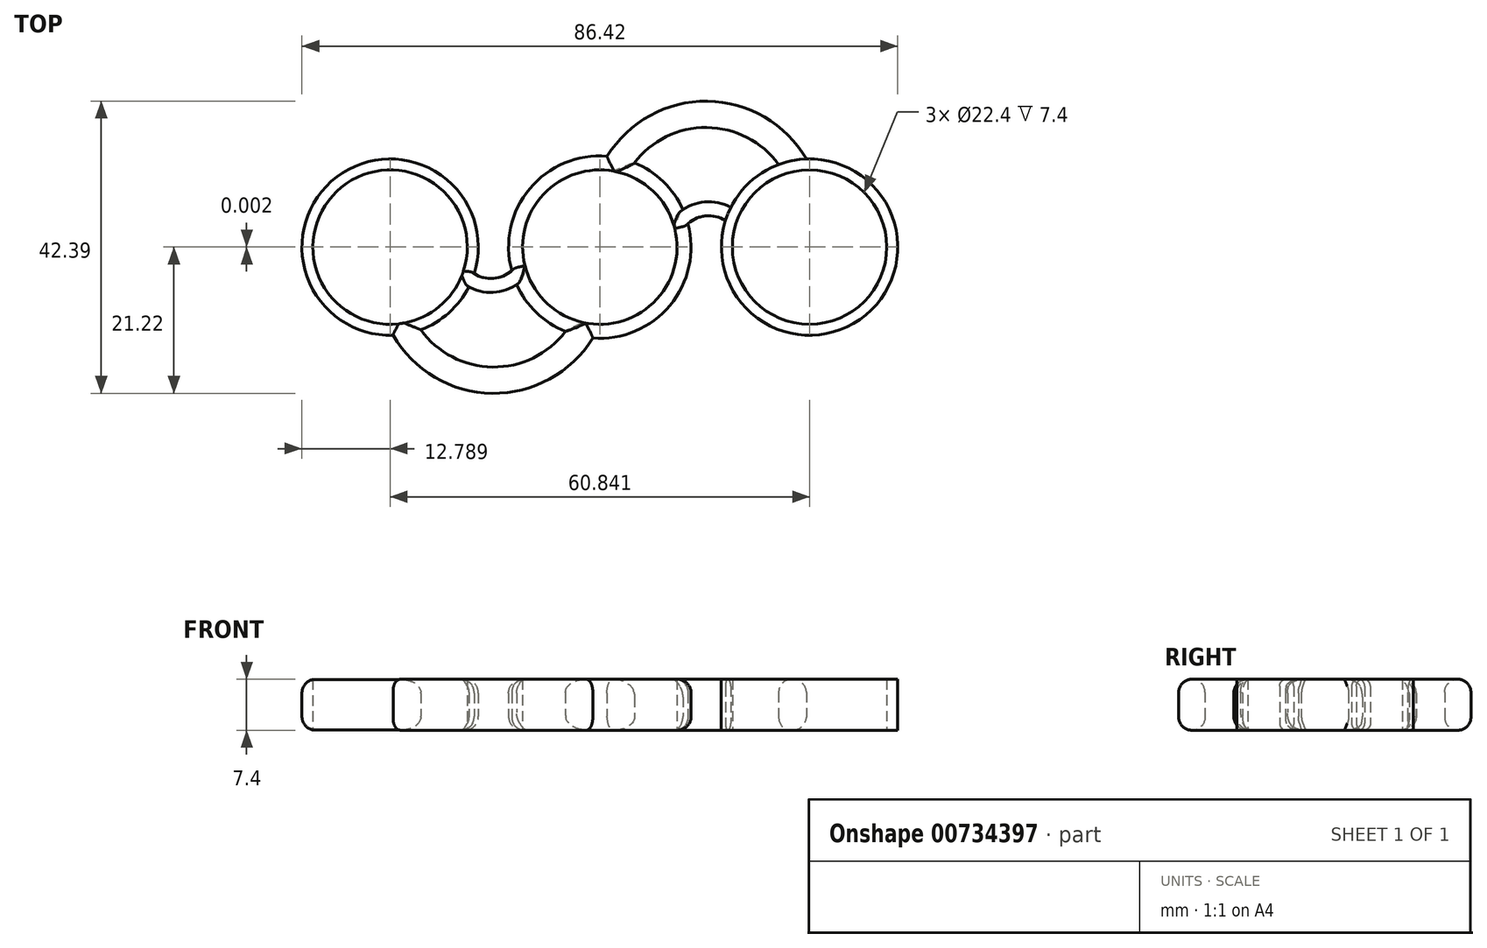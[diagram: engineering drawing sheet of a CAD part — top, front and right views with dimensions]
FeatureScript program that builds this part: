
annotation { "Feature Type Name" : "Feature", "Feature Type Description" : "" }
export const myFeature = defineFeature(function(context is Context, id is Id, definition is map)
    precondition{}
    {
        {
            var Q0;
            Q0=qCreatedBy(makeId("Top.planeOp"),FACE);
            var sketch = newSketch(context, id + "F0", { "sketchPlane" : qUnion([Q0])});
            skCircle(sketch, "E0", {"center": v(0, 0) * mm, "radius": 11.2 * mm});
            skArc(sketch, "E1", {"start": v(-22.34, -1.14) * mm, "mid": v(-15.23, -6.55) * mm, "end": v(-9.15, 0) * mm});
            skArc(sketch, "E2.0", {"start": v(-20.42, 0.11) * mm, "mid": v(-15.8, -4.55) * mm, "end": v(-11.18, 0.11) * mm});
            skLineSegment(sketch, "E3", {"start": v(0, 34.2) * mm, "end": v(0, -29.02) * mm});
            skArc(sketch, "E4.MirrorCS", {"start": v(20.42, 0.11) * mm, "mid": v(20.42, 0.06) * mm, "end": v(20.42, 0) * mm});
            skLineSegment(sketch, "E5", {"start": v(-20.42, 0.11) * mm, "end": v(-22.45, 0) * mm});
            skLineSegment(sketch, "E6", {"start": v(-11.18, 0.11) * mm, "end": v(-9.15, 0) * mm});
            skLineSegment(sketch, "E7", {"start": v(9.15, 0) * mm, "end": v(11.2, 0) * mm});
            skArc(sketch, "E8.MirrorCS", {"start": v(20.42, -0.11) * mm, "mid": v(15.8, 4.55) * mm, "end": v(11.18, -0.11) * mm});
            skArc(sketch, "E9.MirrorCS", {"start": v(22.34, 1.14) * mm, "mid": v(15.23, 6.55) * mm, "end": v(9.15, 0) * mm});
            skLineSegment(sketch, "E10.trimOffspring", {"start": v(19.66, 0) * mm, "end": v(22.45, 0) * mm});
            skPoint(sketch, "E11.orphan", {"position": v(7.21, 0) * mm});
            skArc(sketch, "E12.trimOffspring", {"start": v(11.2, -0.32) * mm, "mid": v(11.18, -0.1) * mm, "end": v(11.18, 0.11) * mm});
            skPoint(sketch, "E13.MirrorCS.start.orphan", {"position": v(22.45, 0) * mm});
            skPoint(sketch, "E14.trimOffspring.end.orphan", {"position": v(9.15, 0) * mm});
            skArc(sketch, "E15", {"start": v(30.99, 10.7) * mm, "mid": v(15.66, 21.17) * mm, "end": v(0, 11.2) * mm});
            skArc(sketch, "E16.0", {"start": v(27.46, 9.25) * mm, "mid": v(15.6, 17.36) * mm, "end": v(3.48, 9.64) * mm});
            skArc(sketch, "E17.MirrorCS", {"start": v(-27.46, -9.3) * mm, "mid": v(-15.6, -17.4) * mm, "end": v(-3.48, -9.7) * mm});
            skArc(sketch, "E18.MirrorCS", {"start": v(-30.99, -10.74) * mm, "mid": v(-15.66, -21.22) * mm, "end": v(0, -11.25) * mm});
            skCircle(sketch, "E19.0", {"center": v(0, 0) * mm, "radius": 13.23 * mm});
            skCircle(sketch, "E20.0", {"center": v(-30.42, 0) * mm, "radius": 12.8 * mm});
            skCircle(sketch, "E21.0", {"center": v(30.42, 0) * mm, "radius": 12.8 * mm});
            skPoint(sketch, "E22.0.midPoint", {"position": v(-30.42, 7.25) * mm});
            skLineSegment(sketch, "E23.5", {"start": v(21.85, 0.3) * mm, "end": v(22.34, 1.14) * mm});
            skPoint(sketch, "E23.0.midPoint", {"position": v(30.24, 7.25) * mm});
            skPoint(sketch, "E23.cCircle.center.orphan", {"position": v(30.24, -0.16) * mm});
            skPoint(sketch, "E23.0.start.orphan", {"position": v(26.13, 7.7) * mm});
            skPoint(sketch, "E23.1.start.orphan", {"position": v(34.35, 6.8) * mm});
            skCircle(sketch, "E24.cCircle", {"center": v(-30.42, 0) * mm, "radius": 7.25 * mm, "construction": true});
            skLineSegment(sketch, "E24.0", {"start": v(-34.6, 7.25) * mm, "end": v(-26.23, 7.25) * mm});
            skLineSegment(sketch, "E24.1", {"start": v(-26.23, 7.25) * mm, "end": v(-22.05, 0) * mm});
            skLineSegment(sketch, "E24.2", {"start": v(-22.05, 0) * mm, "end": v(-26.23, -7.25) * mm});
            skLineSegment(sketch, "E24.3", {"start": v(-26.23, -7.25) * mm, "end": v(-34.6, -7.25) * mm});
            skLineSegment(sketch, "E24.4", {"start": v(-34.6, -7.25) * mm, "end": v(-38.8, 0) * mm});
            skLineSegment(sketch, "E24.5", {"start": v(-38.8, 0) * mm, "end": v(-34.6, 7.25) * mm});
            skCircle(sketch, "E25.cCircle", {"center": v(30.42, 0) * mm, "radius": 7.25 * mm, "construction": true});
            skLineSegment(sketch, "E25.0", {"start": v(26.05, 7.15) * mm, "end": v(34.42, 7.35) * mm});
            skLineSegment(sketch, "E25.1", {"start": v(34.42, 7.35) * mm, "end": v(38.79, 0.21) * mm});
            skLineSegment(sketch, "E25.2", {"start": v(38.79, 0.21) * mm, "end": v(34.79, -7.14) * mm});
            skLineSegment(sketch, "E25.3", {"start": v(34.79, -7.14) * mm, "end": v(26.42, -7.35) * mm});
            skLineSegment(sketch, "E25.4", {"start": v(26.42, -7.35) * mm, "end": v(22.05, -0.2) * mm});
            skLineSegment(sketch, "E25.5", {"start": v(22.05, -0.2) * mm, "end": v(26.05, 7.15) * mm});
            skCircle(sketch, "E26", {"center": v(-30.42, 0) * mm, "radius": 11.2 * mm});
            skCircle(sketch, "E27", {"center": v(30.42, 0) * mm, "radius": 11.2 * mm});
            skSolve(sketch);
        }
        {
            var Q0;
            {var subQ0=sQuery(id+"F0.wireOp",EDGE,"E20.0");var subQ1=sQuery(id+"F0.wireOp",EDGE,"E17.MirrorCS");var subQ2=makeQuery(id+"F0.imprint","INTERSECT",VERTEX,{"derivedFrom":[subQ1,subQ0]});Q0=makeQuery(id+"F0.imprint","IMPRINT",FACE,{"disambiguationData":[TD([[makeQuery(id+"F0.imprint","IMPRINT",EDGE,{"disambiguationData":[TD([[subQ2,-1.0]])],"derivedFrom":subQ1}),-1.0]])]});}
            var Q1;
            {var subQ0=sQuery(id+"F0.wireOp",EDGE,"E2.0");var subQ1=sQuery(id+"F0.wireOp",EDGE,"E0");var subQ2=makeQuery(id+"F0.imprint","INTERSECT",VERTEX,{"derivedFrom":[subQ1,subQ0]});Q1=makeQuery(id+"F0.imprint","IMPRINT",FACE,{"disambiguationData":[TD([[makeQuery(id+"F0.imprint","IMPRINT",EDGE,{"disambiguationData":[TD([[subQ2,-1.0]])],"derivedFrom":subQ1}),-1.0]])]});}
            var Q2;
            {var subQ3=sQuery(id+"F0.wireOp",EDGE,"E2.0");var subQ5=sQuery(id+"F0.wireOp",EDGE,"E19.0");var subQ6=makeQuery(id+"F0.imprint","INTERSECT",VERTEX,{"derivedFrom":[subQ3,subQ5]});Q2=makeQuery(id+"F0.imprint","IMPRINT",FACE,{"disambiguationData":[TD([[makeQuery(id+"F0.imprint","IMPRINT",EDGE,{"disambiguationData":[TD([[subQ6,-1.0]])],"derivedFrom":subQ3}),1.0]])]});}
            var Q3;
            {var subQ0=sQuery(id+"F0.wireOp",EDGE,"E16.0");var subQ1=sQuery(id+"F0.wireOp",EDGE,"E0");var subQ2=makeQuery(id+"F0.imprint","INTERSECT",VERTEX,{"derivedFrom":[subQ1,subQ0]});Q3=makeQuery(id+"F0.imprint","IMPRINT",FACE,{"disambiguationData":[TD([[makeQuery(id+"F0.imprint","IMPRINT",EDGE,{"disambiguationData":[TD([[subQ2,1.0]])],"derivedFrom":subQ1}),-1.0]])]});}
            var Q4;
            {var subQ0=sQuery(id+"F0.wireOp",EDGE,"E8.MirrorCS");var subQ1=sQuery(id+"F0.wireOp",EDGE,"E0");var subQ2=makeQuery(id+"F0.imprint","INTERSECT",VERTEX,{"derivedFrom":[subQ1,subQ0]});Q4=makeQuery(id+"F0.imprint","IMPRINT",FACE,{"disambiguationData":[TD([[makeQuery(id+"F0.imprint","IMPRINT",EDGE,{"disambiguationData":[TD([[subQ2,-1.0]])],"derivedFrom":subQ1}),-1.0]])]});}
            var Q5;
            {var subQ1=sQuery(id+"F0.wireOp",EDGE,"E0");var subQ3=sQuery(id+"F0.wireOp",EDGE,"E17.MirrorCS");var subQ4=makeQuery(id+"F0.imprint","INTERSECT",VERTEX,{"derivedFrom":[subQ1,subQ3]});Q5=makeQuery(id+"F0.imprint","IMPRINT",FACE,{"disambiguationData":[TD([[makeQuery(id+"F0.imprint","IMPRINT",EDGE,{"disambiguationData":[TD([[subQ4,1.0]])],"derivedFrom":subQ3}),-1.0]])]});}
            var Q6;
            {var subQ0=sQuery(id+"F0.wireOp",EDGE,"E17.MirrorCS");var subQ1=sQuery(id+"F0.wireOp",EDGE,"E0");var subQ2=makeQuery(id+"F0.imprint","INTERSECT",VERTEX,{"derivedFrom":[subQ1,subQ0]});Q6=makeQuery(id+"F0.imprint","IMPRINT",FACE,{"disambiguationData":[TD([[makeQuery(id+"F0.imprint","IMPRINT",EDGE,{"disambiguationData":[TD([[subQ2,1.0]])],"derivedFrom":subQ1}),-1.0]])]});}
            var Q7;
            {var subQ0=sQuery(id+"F0.wireOp",EDGE,"E0");var subQ1=makeQuery(id+"F0.imprint","INTERSECT",VERTEX,{"derivedFrom":[subQ0,sQuery(id+"F0.wireOp",EDGE,"E7")]});Q7=makeQuery(id+"F0.imprint","IMPRINT",FACE,{"disambiguationData":[TD([[makeQuery(id+"F0.imprint","IMPRINT",EDGE,{"disambiguationData":[TD([[subQ1,-1.0]])],"derivedFrom":subQ0}),-1.0]])]});}
            var Q8;
            {var subQ1=sQuery(id+"F0.wireOp",EDGE,"E3");var subQ3=sQuery(id+"F0.wireOp",EDGE,"E19.0");var subQ4=makeQuery(id+"F0.imprint","INTERSECT",VERTEX,{"disambiguationData":[OD(1.0)],"derivedFrom":[subQ1,subQ3]});Q8=makeQuery(id+"F0.imprint","IMPRINT",FACE,{"disambiguationData":[TD([[makeQuery(id+"F0.imprint","IMPRINT",EDGE,{"disambiguationData":[TD([[subQ4,1.0]])],"derivedFrom":subQ3}),1.0]])]});}
            var Q9;
            {var subQ1=sQuery(id+"F0.wireOp",EDGE,"E0");var subQ3=sQuery(id+"F0.wireOp",EDGE,"E16.0");var subQ4=makeQuery(id+"F0.imprint","INTERSECT",VERTEX,{"derivedFrom":[subQ1,subQ3]});Q9=makeQuery(id+"F0.imprint","IMPRINT",FACE,{"disambiguationData":[TD([[makeQuery(id+"F0.imprint","IMPRINT",EDGE,{"disambiguationData":[TD([[subQ4,1.0]])],"derivedFrom":subQ3}),-1.0]])]});}
            var Q10;
            {var subQ1=sQuery(id+"F0.wireOp",EDGE,"E3");var subQ3=sQuery(id+"F0.wireOp",EDGE,"E19.0");var subQ4=makeQuery(id+"F0.imprint","INTERSECT",VERTEX,{"disambiguationData":[OD(0.0)],"derivedFrom":[subQ1,subQ3]});Q10=makeQuery(id+"F0.imprint","IMPRINT",FACE,{"disambiguationData":[TD([[makeQuery(id+"F0.imprint","IMPRINT",EDGE,{"disambiguationData":[TD([[subQ4,1.0]])],"derivedFrom":subQ3}),1.0]])]});}
            var Q11;
            {var subQ0=sQuery(id+"F0.wireOp",EDGE,"E21.0");var subQ1=sQuery(id+"F0.wireOp",EDGE,"E15");var subQ2=makeQuery(id+"F0.imprint","INTERSECT",VERTEX,{"derivedFrom":[subQ1,subQ0]});Q11=makeQuery(id+"F0.imprint","IMPRINT",FACE,{"disambiguationData":[TD([[makeQuery(id+"F0.imprint","IMPRINT",EDGE,{"disambiguationData":[TD([[subQ2,-1.0]])],"derivedFrom":subQ1}),1.0]])]});}
            var Q12;
            {var subQ0=sQuery(id+"F0.wireOp",EDGE,"E23.5");Q12=makeQuery(id+"F0.imprint","IMPRINT",FACE,{"disambiguationData":[TD([[makeQuery(id+"F0.imprint","IMPRINT",EDGE,{"derivedFrom":subQ0}),-1.0]])]});}
            var Q13;
            {var subQ7=sQuery(id+"F0.wireOp",EDGE,"E23.5");Q13=makeQuery(id+"F0.imprint","IMPRINT",FACE,{"disambiguationData":[TD([[makeQuery(id+"F0.imprint","IMPRINT",EDGE,{"derivedFrom":subQ7}),1.0]])]});}
            var Q14;
            {var subQ0=sQuery(id+"F0.wireOp",EDGE,"E21.0");var subQ1=sQuery(id+"F0.wireOp",EDGE,"E8.MirrorCS");var subQ2=makeQuery(id+"F0.imprint","INTERSECT",VERTEX,{"derivedFrom":[subQ1,subQ0]});Q14=makeQuery(id+"F0.imprint","IMPRINT",FACE,{"disambiguationData":[TD([[makeQuery(id+"F0.imprint","IMPRINT",EDGE,{"disambiguationData":[TD([[subQ2,-1.0]])],"derivedFrom":subQ1}),-1.0]])]});}
            var Q15;
            {var subQ0=sQuery(id+"F0.wireOp",EDGE,"E20.0");var subQ1=sQuery(id+"F0.wireOp",EDGE,"E1");var subQ2=makeQuery(id+"F0.imprint","INTERSECT",VERTEX,{"derivedFrom":[subQ1,subQ0]});Q15=makeQuery(id+"F0.imprint","IMPRINT",FACE,{"disambiguationData":[TD([[makeQuery(id+"F0.imprint","IMPRINT",EDGE,{"disambiguationData":[TD([[subQ2,-1.0]])],"derivedFrom":subQ1}),1.0]])]});}
            var Q16;
            {var subQ0=sQuery(id+"F0.wireOp",EDGE,"E26");var subQ1=sQuery(id+"F0.wireOp",EDGE,"E1");var subQ2=makeQuery(id+"F0.imprint","INTERSECT",VERTEX,{"derivedFrom":[subQ1,subQ0]});Q16=makeQuery(id+"F0.imprint","IMPRINT",FACE,{"disambiguationData":[TD([[makeQuery(id+"F0.imprint","IMPRINT",EDGE,{"disambiguationData":[TD([[subQ2,-1.0]])],"derivedFrom":subQ1}),1.0]])]});}
            var Q17;
            {var subQ0=sQuery(id+"F0.wireOp",EDGE,"E26");var subQ1=sQuery(id+"F0.wireOp",EDGE,"E1");var subQ2=makeQuery(id+"F0.imprint","INTERSECT",VERTEX,{"derivedFrom":[subQ1,subQ0]});Q17=makeQuery(id+"F0.imprint","IMPRINT",FACE,{"disambiguationData":[TD([[makeQuery(id+"F0.imprint","IMPRINT",EDGE,{"disambiguationData":[TD([[subQ2,-1.0]])],"derivedFrom":subQ1}),-1.0]])]});}
            var Q18;
            {var subQ0=sQuery(id+"F0.wireOp",EDGE,"E26");var subQ1=sQuery(id+"F0.wireOp",EDGE,"E17.MirrorCS");var subQ2=makeQuery(id+"F0.imprint","INTERSECT",VERTEX,{"derivedFrom":[subQ1,subQ0]});Q18=makeQuery(id+"F0.imprint","IMPRINT",FACE,{"disambiguationData":[TD([[makeQuery(id+"F0.imprint","IMPRINT",EDGE,{"disambiguationData":[TD([[subQ2,-1.0]])],"derivedFrom":subQ1}),-1.0]])]});}
            var Q19;
            {var subQ0=sQuery(id+"F0.wireOp",EDGE,"E20.0");var subQ1=sQuery(id+"F0.wireOp",EDGE,"E2.0");var subQ2=makeQuery(id+"F0.imprint","INTERSECT",VERTEX,{"derivedFrom":[subQ1,subQ0]});Q19=makeQuery(id+"F0.imprint","IMPRINT",FACE,{"disambiguationData":[TD([[makeQuery(id+"F0.imprint","IMPRINT",EDGE,{"disambiguationData":[TD([[subQ2,1.0]])],"derivedFrom":subQ1}),1.0]])]});}
            var Q20;
            {var subQ0=sQuery(id+"F0.wireOp",EDGE,"E21.0");var subQ1=sQuery(id+"F0.wireOp",EDGE,"E8.MirrorCS");var subQ2=makeQuery(id+"F0.imprint","INTERSECT",VERTEX,{"derivedFrom":[subQ1,subQ0]});Q20=makeQuery(id+"F0.imprint","IMPRINT",FACE,{"disambiguationData":[TD([[makeQuery(id+"F0.imprint","IMPRINT",EDGE,{"disambiguationData":[TD([[subQ2,1.0]])],"derivedFrom":subQ1}),-1.0]])]});}
            var Q21;
            {var subQ0=sQuery(id+"F0.wireOp",EDGE,"E21.0");var subQ1=sQuery(id+"F0.wireOp",EDGE,"E15");var subQ2=makeQuery(id+"F0.imprint","INTERSECT",VERTEX,{"derivedFrom":[subQ1,subQ0]});Q21=makeQuery(id+"F0.imprint","IMPRINT",FACE,{"disambiguationData":[TD([[makeQuery(id+"F0.imprint","IMPRINT",EDGE,{"disambiguationData":[TD([[subQ2,1.0]])],"derivedFrom":subQ1}),1.0]])]});}
            var Q22;
            {var subQ0=sQuery(id+"F0.wireOp",EDGE,"E27");var subQ1=sQuery(id+"F0.wireOp",EDGE,"E9.MirrorCS");var subQ2=makeQuery(id+"F0.imprint","INTERSECT",VERTEX,{"derivedFrom":[subQ1,subQ0]});Q22=makeQuery(id+"F0.imprint","IMPRINT",FACE,{"disambiguationData":[TD([[makeQuery(id+"F0.imprint","IMPRINT",EDGE,{"disambiguationData":[TD([[subQ2,-1.0]])],"derivedFrom":subQ1}),-1.0]])]});}
            var Q23;
            {var subQ0=sQuery(id+"F0.wireOp",EDGE,"E21.0");var subQ1=sQuery(id+"F0.wireOp",EDGE,"E8.MirrorCS");var subQ2=makeQuery(id+"F0.imprint","INTERSECT",VERTEX,{"derivedFrom":[subQ1,subQ0]});Q23=makeQuery(id+"F0.imprint","IMPRINT",FACE,{"disambiguationData":[TD([[makeQuery(id+"F0.imprint","IMPRINT",EDGE,{"disambiguationData":[TD([[subQ2,1.0]])],"derivedFrom":subQ1}),1.0]])]});}
            extrude(context, id + "F1", {"entities" : qUnion([Q0, Q1, Q2, Q3, Q4, Q5, Q6, Q7, Q8, Q9, Q10, Q11, Q12, Q13, Q14, Q15, Q16, Q17, Q18, Q19, Q20, Q21, Q22, Q23]), "depth" : 7.4 * mm, "offsetDistance" : 25.4 * mm});
        }
        {
            var Q0;
            {var subQ0=sQuery(id+"F0.wireOp",EDGE,"E20.0");Q0=makeQuery(id+"F1.opExtrude","CAP_EDGE",EDGE,{"disambiguationData":[OSD([subQ0]),TDD([makeQuery(id+"F0.imprint","IMPRINT",EDGE,{"disambiguationData":[TD([[makeQuery(id+"F0.imprint","INTERSECT",VERTEX,{"derivedFrom":[sQuery(id+"F0.wireOp",EDGE,"E2.0"),subQ0]}),-1.0]])],"derivedFrom":subQ0})])],"isStart":false});}
            var Q1;
            {var subQ0=sQuery(id+"F0.wireOp",EDGE,"E20.0");Q1=makeQuery(id+"F1.opExtrude","CAP_EDGE",EDGE,{"disambiguationData":[OSD([subQ0]),TDD([makeQuery(id+"F0.imprint","IMPRINT",EDGE,{"disambiguationData":[TD([[makeQuery(id+"F0.imprint","INTERSECT",VERTEX,{"derivedFrom":[sQuery(id+"F0.wireOp",EDGE,"E2.0"),subQ0]}),-1.0]])],"derivedFrom":subQ0})])],"isStart":true});}
            var Q2;
            {var subQ0=sQuery(id+"F0.wireOp",EDGE,"E19.0");Q2=makeQuery(id+"F1.opExtrude","CAP_EDGE",EDGE,{"disambiguationData":[OSD([subQ0]),TDD([makeQuery(id+"F0.imprint","IMPRINT",EDGE,{"disambiguationData":[TD([[makeQuery(id+"F0.imprint","INTERSECT",VERTEX,{"derivedFrom":[sQuery(id+"F0.wireOp",EDGE,"E1"),subQ0]}),-1.0]])],"derivedFrom":subQ0})])],"isStart":false});}
            var Q3;
            {var subQ0=sQuery(id+"F0.wireOp",EDGE,"E19.0");var subQ1=makeQuery(id+"F0.imprint","INTERSECT",VERTEX,{"disambiguationData":[OD(0.0)],"derivedFrom":[sQuery(id+"F0.wireOp",EDGE,"E3"),subQ0]});Q3=makeQuery(id+"F1.opExtrude","CAP_EDGE",EDGE,{"disambiguationData":[OSD([subQ0]),TDD([makeQuery(id+"F0.imprint","IMPRINT",EDGE,{"disambiguationData":[TD([[subQ1,1.0]])],"derivedFrom":subQ0}),makeQuery(id+"F0.imprint","IMPRINT",EDGE,{"disambiguationData":[TD([[subQ1,-1.0]])],"derivedFrom":subQ0})])],"isStart":false});}
            var Q4;
            {var subQ0=sQuery(id+"F0.wireOp",EDGE,"E19.0");var subQ1=makeQuery(id+"F0.imprint","INTERSECT",VERTEX,{"disambiguationData":[OD(1.0)],"derivedFrom":[sQuery(id+"F0.wireOp",EDGE,"E3"),subQ0]});Q4=makeQuery(id+"F1.opExtrude","CAP_EDGE",EDGE,{"disambiguationData":[OSD([subQ0]),TDD([makeQuery(id+"F0.imprint","IMPRINT",EDGE,{"disambiguationData":[TD([[subQ1,1.0]])],"derivedFrom":subQ0}),makeQuery(id+"F0.imprint","IMPRINT",EDGE,{"disambiguationData":[TD([[subQ1,-1.0]])],"derivedFrom":subQ0})])],"isStart":false});}
            var Q5;
            {var subQ0=sQuery(id+"F0.wireOp",EDGE,"E19.0");var subQ1=makeQuery(id+"F0.imprint","INTERSECT",VERTEX,{"disambiguationData":[OD(1.0)],"derivedFrom":[sQuery(id+"F0.wireOp",EDGE,"E3"),subQ0]});Q5=makeQuery(id+"F1.opExtrude","CAP_EDGE",EDGE,{"disambiguationData":[OSD([subQ0]),TDD([makeQuery(id+"F0.imprint","IMPRINT",EDGE,{"disambiguationData":[TD([[subQ1,1.0]])],"derivedFrom":subQ0}),makeQuery(id+"F0.imprint","IMPRINT",EDGE,{"disambiguationData":[TD([[subQ1,-1.0]])],"derivedFrom":subQ0})])],"isStart":true});}
            var Q6;
            {var subQ0=sQuery(id+"F0.wireOp",EDGE,"E21.0");Q6=makeQuery(id+"F1.opExtrude","CAP_EDGE",EDGE,{"disambiguationData":[OSD([subQ0]),TDD([makeQuery(id+"F0.imprint","IMPRINT",EDGE,{"disambiguationData":[TD([[makeQuery(id+"F0.imprint","INTERSECT",VERTEX,{"derivedFrom":[sQuery(id+"F0.wireOp",EDGE,"E15"),subQ0]}),-1.0]])],"derivedFrom":subQ0})])],"isStart":false});}
            var Q7;
            {var subQ0=sQuery(id+"F0.wireOp",EDGE,"E21.0");Q7=makeQuery(id+"F1.opExtrude","CAP_EDGE",EDGE,{"disambiguationData":[OSD([subQ0]),TDD([makeQuery(id+"F0.imprint","IMPRINT",EDGE,{"disambiguationData":[TD([[makeQuery(id+"F0.imprint","INTERSECT",VERTEX,{"derivedFrom":[sQuery(id+"F0.wireOp",EDGE,"E15"),subQ0]}),-1.0]])],"derivedFrom":subQ0})])],"isStart":true});}
            var Q8;
            {var subQ0=sQuery(id+"F0.wireOp",EDGE,"E21.0");Q8=makeQuery(id+"F1.opExtrude","CAP_EDGE",EDGE,{"disambiguationData":[OSD([subQ0]),TDD([makeQuery(id+"F0.imprint","IMPRINT",EDGE,{"disambiguationData":[TD([[makeQuery(id+"F0.imprint","INTERSECT",VERTEX,{"derivedFrom":[sQuery(id+"F0.wireOp",EDGE,"E16.0"),subQ0]}),1.0]])],"derivedFrom":subQ0})])],"isStart":true});}
            var Q9;
            {var subQ0=sQuery(id+"F0.wireOp",EDGE,"E19.0");var subQ1=makeQuery(id+"F0.imprint","INTERSECT",VERTEX,{"disambiguationData":[OD(0.0)],"derivedFrom":[sQuery(id+"F0.wireOp",EDGE,"E3"),subQ0]});Q9=makeQuery(id+"F1.opExtrude","CAP_EDGE",EDGE,{"disambiguationData":[OSD([subQ0]),TDD([makeQuery(id+"F0.imprint","IMPRINT",EDGE,{"disambiguationData":[TD([[subQ1,1.0]])],"derivedFrom":subQ0}),makeQuery(id+"F0.imprint","IMPRINT",EDGE,{"disambiguationData":[TD([[subQ1,-1.0]])],"derivedFrom":subQ0})])],"isStart":true});}
            var Q10;
            {var subQ0=sQuery(id+"F0.wireOp",EDGE,"E20.0");Q10=makeQuery(id+"F1.opExtrude","CAP_EDGE",EDGE,{"disambiguationData":[OSD([subQ0]),TDD([makeQuery(id+"F0.imprint","IMPRINT",EDGE,{"disambiguationData":[TD([[makeQuery(id+"F0.imprint","INTERSECT",VERTEX,{"derivedFrom":[sQuery(id+"F0.wireOp",EDGE,"E1"),subQ0]}),1.0]])],"derivedFrom":subQ0})])],"isStart":false});}
            var Q11;
            {var subQ0=sQuery(id+"F0.wireOp",EDGE,"E21.0");Q11=makeQuery(id+"F1.opExtrude","CAP_EDGE",EDGE,{"disambiguationData":[OSD([subQ0]),TDD([makeQuery(id+"F0.imprint","IMPRINT",EDGE,{"disambiguationData":[TD([[makeQuery(id+"F0.imprint","INTERSECT",VERTEX,{"derivedFrom":[sQuery(id+"F0.wireOp",EDGE,"E16.0"),subQ0]}),1.0]])],"derivedFrom":subQ0})])],"isStart":false});}
            var Q12;
            {var subQ0=sQuery(id+"F0.wireOp",EDGE,"E20.0");Q12=makeQuery(id+"F1.opExtrude","CAP_EDGE",EDGE,{"disambiguationData":[OSD([subQ0]),TDD([makeQuery(id+"F0.imprint","IMPRINT",EDGE,{"disambiguationData":[TD([[makeQuery(id+"F0.imprint","INTERSECT",VERTEX,{"derivedFrom":[sQuery(id+"F0.wireOp",EDGE,"E1"),subQ0]}),1.0]])],"derivedFrom":subQ0})])],"isStart":true});}
            var Q13;
            {var subQ0=sQuery(id+"F0.wireOp",EDGE,"E19.0");Q13=makeQuery(id+"F1.opExtrude","CAP_EDGE",EDGE,{"disambiguationData":[OSD([subQ0]),TDD([makeQuery(id+"F0.imprint","IMPRINT",EDGE,{"disambiguationData":[TD([[makeQuery(id+"F0.imprint","INTERSECT",VERTEX,{"derivedFrom":[sQuery(id+"F0.wireOp",EDGE,"E9.MirrorCS"),subQ0]}),-1.0]])],"derivedFrom":subQ0})])],"isStart":true});}
            fillet(context, id + "F2", {"entities" : qUnion([Q0, Q1, Q2, Q3, Q4, Q5, Q6, Q7, Q8, Q9, Q10, Q11, Q12, Q13]), "radius" : 2 * mm, "tangentPropagation" : true, "allowEdgeOverflow" : false});
        }
        {
            var Q0;
            Q0=makeQuery(id+"F1.opExtrude","CAP_EDGE",EDGE,{"disambiguationData":[OSD([sQuery(id+"F0.wireOp",EDGE,"E2.0")])],"isStart":false});
            var Q1;
            Q1=makeQuery(id+"F1.opExtrude","CAP_EDGE",EDGE,{"disambiguationData":[OSD([sQuery(id+"F0.wireOp",EDGE,"E1")])],"isStart":false});
            var Q2;
            Q2=makeQuery(id+"F1.opExtrude","CAP_EDGE",EDGE,{"disambiguationData":[OSD([sQuery(id+"F0.wireOp",EDGE,"E9.MirrorCS")])],"isStart":false});
            var Q3;
            Q3=makeQuery(id+"F1.opExtrude","CAP_EDGE",EDGE,{"disambiguationData":[OSD([sQuery(id+"F0.wireOp",EDGE,"E8.MirrorCS")])],"isStart":false});
            var Q4;
            Q4=makeQuery(id+"F1.opExtrude","CAP_EDGE",EDGE,{"disambiguationData":[OSD([sQuery(id+"F0.wireOp",EDGE,"E9.MirrorCS")])],"isStart":true});
            var Q5;
            Q5=makeQuery(id+"F1.opExtrude","CAP_EDGE",EDGE,{"disambiguationData":[OSD([sQuery(id+"F0.wireOp",EDGE,"E8.MirrorCS")])],"isStart":true});
            var Q6;
            Q6=makeQuery(id+"F1.opExtrude","CAP_EDGE",EDGE,{"disambiguationData":[OSD([sQuery(id+"F0.wireOp",EDGE,"E2.0")])],"isStart":true});
            var Q7;
            Q7=makeQuery(id+"F1.opExtrude","CAP_EDGE",EDGE,{"disambiguationData":[OSD([sQuery(id+"F0.wireOp",EDGE,"E1")])],"isStart":true});
            fillet(context, id + "F3", {"entities" : qUnion([Q0, Q1, Q2, Q3, Q4, Q5, Q6, Q7]), "radius" : 1 * mm, "tangentPropagation" : true, "allowEdgeOverflow" : false});
        }
        {
            var Q0;
            {var subQ0=sQuery(id+"F0.wireOp",EDGE,"E19.0");Q0=makeQuery(id+"F1.opExtrude","CAP_EDGE",EDGE,{"disambiguationData":[OSD([subQ0]),TDD([makeQuery(id+"F0.imprint","IMPRINT",EDGE,{"disambiguationData":[TD([[makeQuery(id+"F0.imprint","INTERSECT",VERTEX,{"derivedFrom":[sQuery(id+"F0.wireOp",EDGE,"E1"),subQ0]}),-1.0]])],"derivedFrom":subQ0})])],"isStart":true});}
            var Q1;
            {var subQ0=sQuery(id+"F0.wireOp",EDGE,"E19.0");Q1=makeQuery(id+"F1.opExtrude","CAP_EDGE",EDGE,{"disambiguationData":[OSD([subQ0]),TDD([makeQuery(id+"F0.imprint","IMPRINT",EDGE,{"disambiguationData":[TD([[makeQuery(id+"F0.imprint","INTERSECT",VERTEX,{"derivedFrom":[sQuery(id+"F0.wireOp",EDGE,"E9.MirrorCS"),subQ0]}),-1.0]])],"derivedFrom":subQ0})])],"isStart":false});}
            fillet(context, id + "F4", {"entities" : qUnion([Q0, Q1]), "radius" : 2.58 * mm, "tangentPropagation" : true, "allowEdgeOverflow" : false});
        }
        {
            var Q0;
            Q0=makeQuery(id+"F1.opExtrude","CAP_EDGE",EDGE,{"disambiguationData":[OSD([sQuery(id+"F0.wireOp",EDGE,"E18.MirrorCS")])],"isStart":true});
            var Q1;
            Q1=makeQuery(id+"F1.opExtrude","CAP_EDGE",EDGE,{"disambiguationData":[OSD([sQuery(id+"F0.wireOp",EDGE,"E17.MirrorCS")])],"isStart":true});
            var Q2;
            Q2=makeQuery(id+"F1.opExtrude","CAP_EDGE",EDGE,{"disambiguationData":[OSD([sQuery(id+"F0.wireOp",EDGE,"E16.0")])],"isStart":true});
            var Q3;
            Q3=makeQuery(id+"F1.opExtrude","CAP_EDGE",EDGE,{"disambiguationData":[OSD([sQuery(id+"F0.wireOp",EDGE,"E15")])],"isStart":true});
            var Q4;
            Q4=makeQuery(id+"F1.opExtrude","CAP_EDGE",EDGE,{"disambiguationData":[OSD([sQuery(id+"F0.wireOp",EDGE,"E17.MirrorCS")])],"isStart":false});
            var Q5;
            Q5=makeQuery(id+"F1.opExtrude","CAP_EDGE",EDGE,{"disambiguationData":[OSD([sQuery(id+"F0.wireOp",EDGE,"E18.MirrorCS")])],"isStart":false});
            var Q6;
            Q6=makeQuery(id+"F1.opExtrude","CAP_EDGE",EDGE,{"disambiguationData":[OSD([sQuery(id+"F0.wireOp",EDGE,"E16.0")])],"isStart":false});
            var Q7;
            Q7=makeQuery(id+"F1.opExtrude","CAP_EDGE",EDGE,{"disambiguationData":[OSD([sQuery(id+"F0.wireOp",EDGE,"E15")])],"isStart":false});
            fillet(context, id + "F5", {"entities" : qUnion([Q0, Q1, Q2, Q3, Q4, Q5, Q6, Q7]), "radius" : 1.88 * mm, "tangentPropagation" : true, "allowEdgeOverflow" : false});
        }
    });
